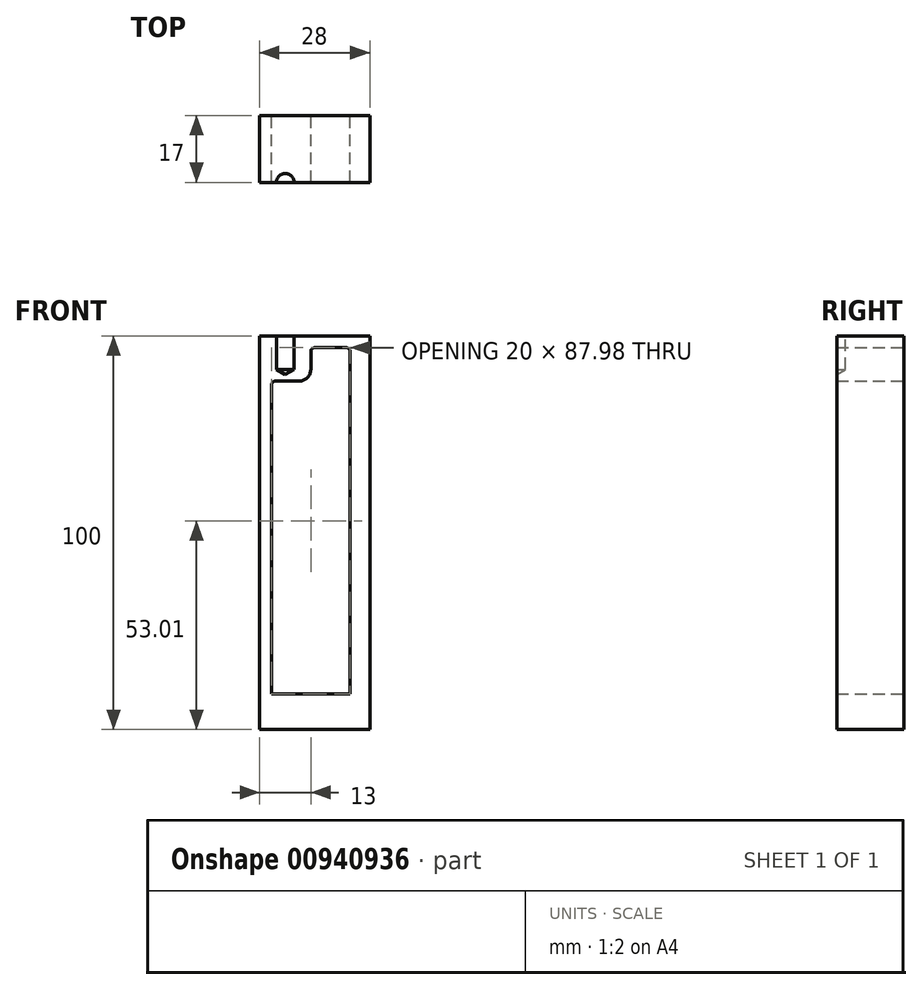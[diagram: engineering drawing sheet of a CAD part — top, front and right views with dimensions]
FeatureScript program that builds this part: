
annotation { "Feature Type Name" : "Feature", "Feature Type Description" : "" }
export const myFeature = defineFeature(function(context is Context, id is Id, definition is map)
    precondition{}
    {
        {
            var Q0;
            Q0=qCreatedBy(makeId("Front.planeOp"),FACE);
            var sketch = newSketch(context, id + "F0", { "sketchPlane" : qUnion([Q0])});
            skLineSegment(sketch, "E0.bottom", {"start": v(0, 0) * mm, "end": v(28, 0) * mm});
            skLineSegment(sketch, "E0.top", {"start": v(0, 100) * mm, "end": v(28, 100) * mm});
            skLineSegment(sketch, "E0.left", {"start": v(0, 0) * mm, "end": v(0, 100) * mm});
            skLineSegment(sketch, "E0.right", {"start": v(28, 0) * mm, "end": v(28, 100) * mm});
            skLineSegment(sketch, "E1.bottom", {"start": v(22, 97) * mm, "end": v(14, 97) * mm});
            skLineSegment(sketch, "E1.top", {"start": v(23, 9.02) * mm, "end": v(3, 9.02) * mm});
            skLineSegment(sketch, "E1.left", {"start": v(23, 96) * mm, "end": v(23, 9.02) * mm});
            skLineSegment(sketch, "E1.right", {"start": v(3, 87.5) * mm, "end": v(3, 9.02) * mm});
            skArc(sketch, "E2", {"start": v(23, 96) * mm, "mid": v(22.7, 96.7) * mm, "end": v(22, 97) * mm});
            skPoint(sketch, "E3.orphan", {"position": v(23, 97) * mm});
            skLineSegment(sketch, "E4", {"start": v(6.5, 103.35) * mm, "end": v(6.5, 90.16) * mm, "construction": true});
            skLineSegment(sketch, "E5", {"start": v(4, 90.16) * mm, "end": v(9, 90.16) * mm, "construction": true});
            skLineSegment(sketch, "E6", {"start": v(9, 90.16) * mm, "end": v(9, 103.35) * mm, "construction": true});
            skLineSegment(sketch, "E7", {"start": v(9, 103.35) * mm, "end": v(4, 103.35) * mm, "construction": true});
            skLineSegment(sketch, "E8", {"start": v(4, 103.35) * mm, "end": v(4, 90.16) * mm, "construction": true});
            skArc(sketch, "E9", {"start": v(4, 88.5) * mm, "mid": v(3.3, 88.2) * mm, "end": v(3, 87.5) * mm});
            skLineSegment(sketch, "E10", {"start": v(4, 88.5) * mm, "end": v(10, 88.5) * mm});
            skArc(sketch, "E11", {"start": v(10, 88.5) * mm, "mid": v(12.12, 89.38) * mm, "end": v(13, 91.5) * mm});
            skLineSegment(sketch, "E12", {"start": v(13, 91.5) * mm, "end": v(13, 96) * mm});
            skArc(sketch, "E13", {"start": v(14, 97) * mm, "mid": v(13.3, 96.7) * mm, "end": v(13, 96) * mm});
            skSolve(sketch);
        }
        {
            var Q0;
            Q0=makeQuery(id+"F0.imprint","IMPRINT",FACE,{"disambiguationData":[TD([[makeQuery(id+"F0.imprint","IMPRINT",EDGE,{"derivedFrom":sQuery(id+"F0.wireOp",EDGE,"E0.bottom")}),1.0]])]});
            extrude(context, id + "F1", {"entities" : qUnion([Q0]), "depth" : 25 * mm, "offsetDistance" : 25 * mm});
        }
        {
            var Q0;
            Q0=makeQuery(id+"F1.opExtrude","SWEPT_FACE",FACE,{"disambiguationData":[OSD([sQuery(id+"F0.wireOp",EDGE,"E0.top")])]});
            var sketch = newSketch(context, id + "F2", { "sketchPlane" : qUnion([Q0])});
            skPoint(sketch, "E14", {"position": v(6.5, -17) * mm});
            skSolve(sketch);
        }
        {
            var Q0;
            Q0=sQuery(id+"F2.wireOp",VERTEX,"E14");
            var Q1;
            Q1=makeQuery(id+"F1.opExtrude","SWEPT_BODY",BODY,{"disambiguationData":[OSD([sQuery(id+"F0.wireOp",EDGE,"E0.bottom"),sQuery(id+"F0.wireOp",EDGE,"E0.top"),sQuery(id+"F0.wireOp",EDGE,"E0.left"),sQuery(id+"F0.wireOp",EDGE,"E0.right"),sQuery(id+"F0.wireOp",EDGE,"E1.bottom"),sQuery(id+"F0.wireOp",EDGE,"E1.top"),sQuery(id+"F0.wireOp",EDGE,"E1.left"),sQuery(id+"F0.wireOp",EDGE,"E1.right"),sQuery(id+"F0.wireOp",EDGE,"E2"),sQuery(id+"F0.wireOp",EDGE,"E9"),sQuery(id+"F0.wireOp",EDGE,"E10"),sQuery(id+"F0.wireOp",EDGE,"E11"),sQuery(id+"F0.wireOp",EDGE,"E12"),sQuery(id+"F0.wireOp",EDGE,"E13")])]});
            hole(context, id + "F3", {"style" : HoleStyle.SIMPLE, "endStyle" : HoleEndStyle.BLIND, "standardTappedOrClearance" : lookupTablePath({ "standard" : "ISO", "size" : "4.5", "type" : "Drilled" }), "standardBlindInLast" : lookupTablePath({ "standard" : "ISO", "size" : "4.5", "type" : "Drilled" }), "holeDiameter" : 4.5 * mm, "majorDiameter" : 5 * mm, "holeDepth" : 8.5 * mm, "isTappedThrough" : true, "tappedDepth" : 12 * mm, "tapClearance" : 3, "locations" : qUnion([Q0]), "scope" : qUnion([Q1])});
        }
        {
            var Q0;
            Q0=makeQuery(id+"F1.opExtrude","SWEPT_FACE",FACE,{"disambiguationData":[OSD([sQuery(id+"F0.wireOp",EDGE,"E0.top")])]});
            var sketch = newSketch(context, id + "F4", { "sketchPlane" : qUnion([Q0])});
            skLineSegment(sketch, "E15.bottom", {"start": v(0, -25) * mm, "end": v(28, -25) * mm});
            skLineSegment(sketch, "E15.top", {"start": v(0, -17) * mm, "end": v(28, -17) * mm});
            skLineSegment(sketch, "E15.left", {"start": v(0, -25) * mm, "end": v(0, -17) * mm});
            skLineSegment(sketch, "E15.right", {"start": v(28, -25) * mm, "end": v(28, -17) * mm});
            skSolve(sketch);
        }
        {
            var Q0;
            Q0 = qSketchRegion(id + "F4", true);
            extrude(context, id + "F5", {"entities" : qUnion([Q0]), "operationType" : NewBodyOperationType.REMOVE, "endBound" : BoundingType.THROUGH_ALL, "oppositeDirection" : true, "depth" : 25 * mm, "offsetDistance" : 25 * mm});
        }
    });
